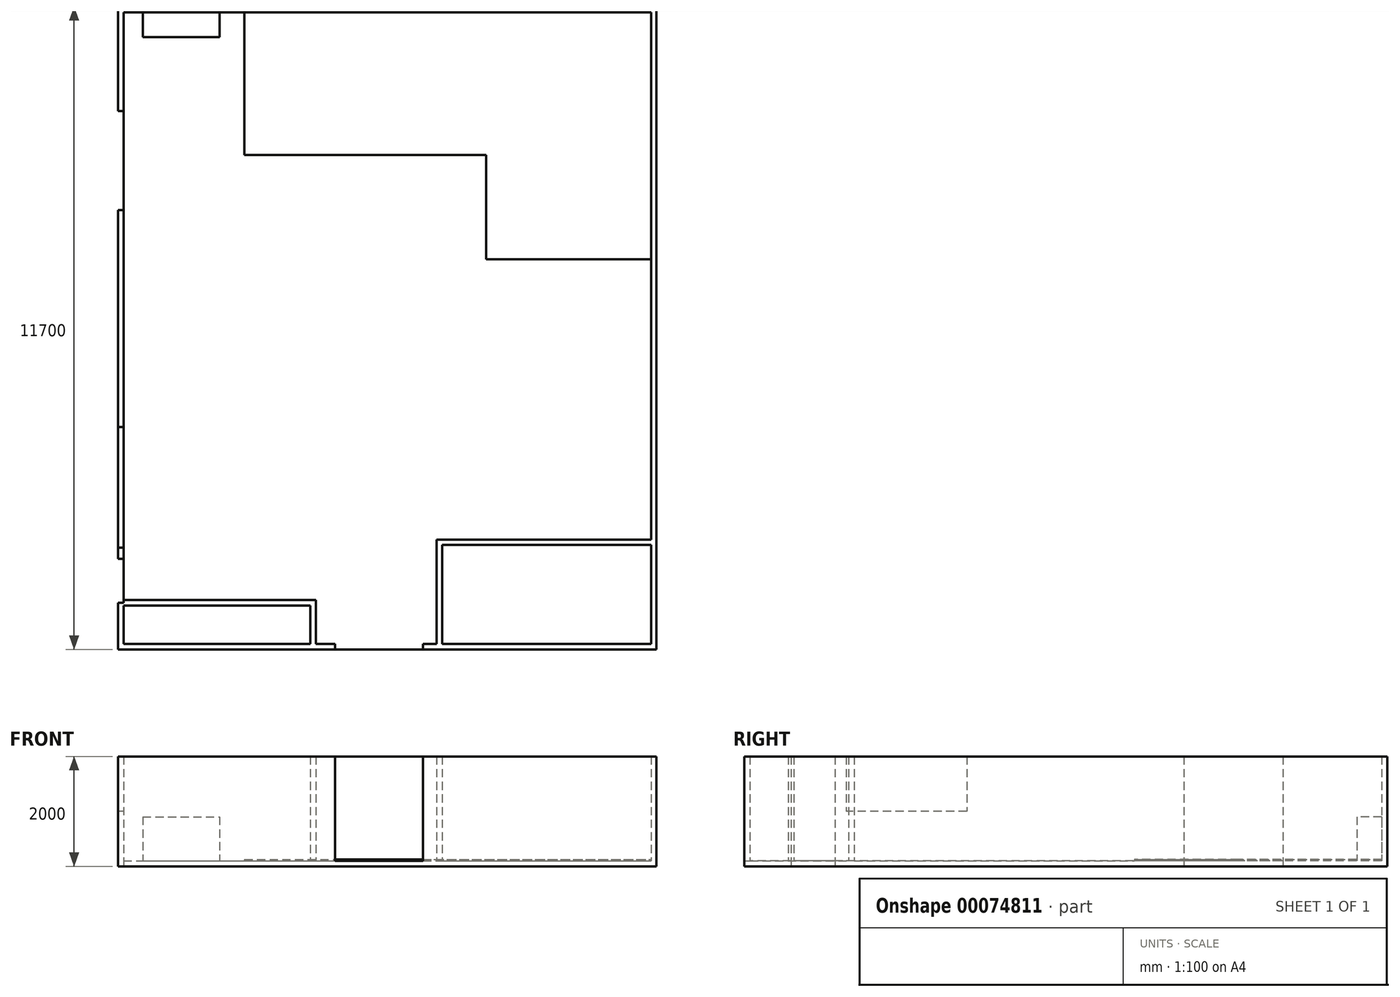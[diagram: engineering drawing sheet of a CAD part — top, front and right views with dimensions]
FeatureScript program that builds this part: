
annotation { "Feature Type Name" : "Feature", "Feature Type Description" : "" }
export const myFeature = defineFeature(function(context is Context, id is Id, definition is map)
    precondition{}
    {
        {
            var Q0;
            Q0=qCreatedBy(makeId("Top.planeOp"),FACE);
            var sketch = newSketch(context, id + "F0", { "sketchPlane" : qUnion([Q0])});
            skLineSegment(sketch, "E0.bottom", {"start": v(-14637.26, 1697.17) * mm, "end": v(-4837.26, 1697.17) * mm});
            skLineSegment(sketch, "E0.top", {"start": v(-14637.26, -10002.83) * mm, "end": v(-4837.26, -10002.83) * mm});
            skLineSegment(sketch, "E0.left", {"start": v(-14637.26, 1697.17) * mm, "end": v(-14637.26, -10002.83) * mm});
            skLineSegment(sketch, "E0.right", {"start": v(-4837.26, 1697.17) * mm, "end": v(-4837.26, -10002.83) * mm});
            skLineSegment(sketch, "E1.top", {"start": v(-8937.26, -10002.83) * mm, "end": v(-4837.26, -10002.83) * mm});
            skLineSegment(sketch, "E1.right", {"start": v(-4837.26, -8102.83) * mm, "end": v(-4837.26, -10002.83) * mm});
            skLineSegment(sketch, "E2.top", {"start": v(-11137.26, -10002.83) * mm, "end": v(-14637.26, -10002.83) * mm});
            skLineSegment(sketch, "E2.right", {"start": v(-14637.26, -9202.83) * mm, "end": v(-14637.26, -10002.83) * mm});
            skSolve(sketch);
        }
        {
            var Q0;
            Q0 = qSketchRegion(id + "F0", true);
            extrude(context, id + "F1", {"entities" : qUnion([Q0]), "depth" : 100 * mm});
        }
        {
            var Q0;
            Q0=makeQuery(id+"F1.opExtrude","CAP_FACE",FACE,{"disambiguationData":[OSD([sQuery(id+"F0.wireOp",EDGE,"E0.bottom"),sQuery(id+"F0.wireOp",EDGE,"E0.top"),sQuery(id+"F0.wireOp",EDGE,"E0.left"),sQuery(id+"F0.wireOp",EDGE,"E0.right"),sQuery(id+"F0.wireOp",EDGE,"E1.top"),sQuery(id+"F0.wireOp",EDGE,"E1.right"),sQuery(id+"F0.wireOp",EDGE,"E2.top"),sQuery(id+"F0.wireOp",EDGE,"E2.right")])],"isStart":false});
            var sketch = newSketch(context, id + "F2", { "sketchPlane" : qUnion([Q0])});
            skLineSegment(sketch, "E3.bottom", {"start": v(-14637.26, -10002.83) * mm, "end": v(-10890.72, -10002.83) * mm});
            skLineSegment(sketch, "E3.left", {"start": v(-14637.26, -10002.83) * mm, "end": v(-14637.26, -9155.58) * mm});
            skLineSegment(sketch, "E4.bottom", {"start": v(-4837.26, -10002.83) * mm, "end": v(-8666.1, -10002.83) * mm});
            skLineSegment(sketch, "E4.left", {"start": v(-4837.26, -10002.83) * mm, "end": v(-4837.26, -7690.3) * mm});
            skLineSegment(sketch, "E5.bottom", {"start": v(-14637.26, 1697.17) * mm, "end": v(-4837.26, 1697.17) * mm});
            skLineSegment(sketch, "E5.top", {"start": v(-14637.26, 1597.17) * mm, "end": v(-4837.26, 1597.17) * mm});
            skLineSegment(sketch, "E5.left", {"start": v(-14637.26, 1697.17) * mm, "end": v(-14637.26, 1597.17) * mm});
            skLineSegment(sketch, "E5.right", {"start": v(-4837.26, 1697.17) * mm, "end": v(-4837.26, 1597.17) * mm});
            skLineSegment(sketch, "E6.bottom", {"start": v(-14637.26, 1597.17) * mm, "end": v(-14537.26, 1597.17) * mm});
            skLineSegment(sketch, "E6.left", {"start": v(-14637.26, 1597.17) * mm, "end": v(-14637.26, -8609.96) * mm});
            skLineSegment(sketch, "E7.top", {"start": v(-5037.26, 1597.17) * mm, "end": v(-4837.26, 1597.17) * mm});
            skLineSegment(sketch, "E7.right", {"start": v(-4837.26, -7344.68) * mm, "end": v(-4837.26, 1597.17) * mm});
            skLineSegment(sketch, "E8.bottom", {"start": v(-14637.26, -10002.83) * mm, "end": v(-4837.26, -10002.83) * mm});
            skLineSegment(sketch, "E8.top", {"start": v(-14637.26, -9902.83) * mm, "end": v(-4837.26, -9902.83) * mm});
            skLineSegment(sketch, "E8.left", {"start": v(-14637.26, -10002.83) * mm, "end": v(-14637.26, -9902.83) * mm});
            skLineSegment(sketch, "E8.right", {"start": v(-4837.26, -10002.83) * mm, "end": v(-4837.26, -9902.83) * mm});
            skLineSegment(sketch, "E9.bottom", {"start": v(-4837.26, -10002.83) * mm, "end": v(-4937.26, -10002.83) * mm});
            skLineSegment(sketch, "E9.top", {"start": v(-4837.26, 1597.17) * mm, "end": v(-4937.26, 1597.17) * mm});
            skLineSegment(sketch, "E9.left", {"start": v(-4837.26, -10002.83) * mm, "end": v(-4837.26, 1597.17) * mm});
            skLineSegment(sketch, "E9.right", {"start": v(-4937.26, -10002.83) * mm, "end": v(-4937.26, 1597.17) * mm});
            skLineSegment(sketch, "E10.top", {"start": v(-14637.26, -9902.83) * mm, "end": v(-14537.26, -9902.83) * mm});
            skLineSegment(sketch, "E10.left", {"start": v(-14637.26, 1597.17) * mm, "end": v(-14637.26, -9902.83) * mm});
            skLineSegment(sketch, "E10.right", {"start": v(-14537.26, 1597.17) * mm, "end": v(-14537.26, -9902.83) * mm});
            skLineSegment(sketch, "E11.top", {"start": v(-14537.26, -9902.83) * mm, "end": v(-11037.26, -9902.83) * mm});
            skLineSegment(sketch, "E11.left", {"start": v(-14537.26, -8902.83) * mm, "end": v(-14537.26, -9902.83) * mm});
            skLineSegment(sketch, "E12.bottom", {"start": v(-9037.26, -9902.83) * mm, "end": v(-4937.26, -9902.83) * mm});
            skLineSegment(sketch, "E12.right", {"start": v(-4937.26, -9902.83) * mm, "end": v(-4937.26, -8002.83) * mm});
            skSolve(sketch);
        }
        {
            var Q0;
            Q0 = qSketchRegion(id + "F2", true);
            extrude(context, id + "F3", {"entities" : qUnion([Q0]), "operationType" : NewBodyOperationType.ADD, "depth" : 1900 * mm});
        }
        {
            var Q0;
            Q0=makeQuery(id+"F1.opExtrude","CAP_FACE",FACE,{"disambiguationData":[OSD([sQuery(id+"F0.wireOp",EDGE,"E0.bottom"),sQuery(id+"F0.wireOp",EDGE,"E0.top"),sQuery(id+"F0.wireOp",EDGE,"E0.left"),sQuery(id+"F0.wireOp",EDGE,"E0.right"),sQuery(id+"F0.wireOp",EDGE,"E1.top"),sQuery(id+"F0.wireOp",EDGE,"E1.right"),sQuery(id+"F0.wireOp",EDGE,"E2.top"),sQuery(id+"F0.wireOp",EDGE,"E2.right")])],"isStart":false});
            var sketch = newSketch(context, id + "F4", { "sketchPlane" : qUnion([Q0])});
            skLineSegment(sketch, "E13.bottom", {"start": v(-8837.26, -8002.83) * mm, "end": v(-8737.26, -8002.83) * mm});
            skLineSegment(sketch, "E13.top", {"start": v(-8837.26, -9902.83) * mm, "end": v(-8737.26, -9902.83) * mm});
            skLineSegment(sketch, "E13.left", {"start": v(-8837.26, -8002.83) * mm, "end": v(-8837.26, -9902.83) * mm});
            skLineSegment(sketch, "E13.right", {"start": v(-8737.26, -8102.83) * mm, "end": v(-8737.26, -9902.83) * mm});
            skLineSegment(sketch, "E14.bottom", {"start": v(-8837.26, -8002.83) * mm, "end": v(-4937.26, -8002.83) * mm});
            skLineSegment(sketch, "E14.top", {"start": v(-8737.26, -8102.83) * mm, "end": v(-4937.26, -8102.83) * mm});
            skLineSegment(sketch, "E14.left", {"start": v(-8837.26, -8102.83) * mm, "end": v(-8837.26, -8002.83) * mm});
            skLineSegment(sketch, "E14.right", {"start": v(-4937.26, -8102.83) * mm, "end": v(-4937.26, -8002.83) * mm});
            skLineSegment(sketch, "E15.bottom", {"start": v(-14537.26, -9102.83) * mm, "end": v(-11137.26, -9102.83) * mm});
            skLineSegment(sketch, "E15.top", {"start": v(-14537.26, -9202.83) * mm, "end": v(-11137.26, -9202.83) * mm});
            skLineSegment(sketch, "E15.left", {"start": v(-14537.26, -9102.83) * mm, "end": v(-14537.26, -9202.83) * mm});
            skLineSegment(sketch, "E16.bottom", {"start": v(-11037.26, -9902.83) * mm, "end": v(-11137.26, -9902.83) * mm});
            skLineSegment(sketch, "E16.top", {"start": v(-11037.26, -9102.83) * mm, "end": v(-11137.26, -9102.83) * mm});
            skLineSegment(sketch, "E16.left", {"start": v(-11037.26, -9902.83) * mm, "end": v(-11037.26, -9102.83) * mm});
            skLineSegment(sketch, "E16.right", {"start": v(-11137.26, -9902.83) * mm, "end": v(-11137.26, -9202.83) * mm});
            skSolve(sketch);
        }
        {
            var Q0;
            Q0=makeQuery(id+"F4.imprint","IMPRINT",FACE,{"disambiguationData":[TD([[makeQuery(id+"F4.imprint","IMPRINT",EDGE,{"derivedFrom":sQuery(id+"F4.wireOp",EDGE,"E15.bottom")}),-1.0]])]});
            var Q1;
            Q1=makeQuery(id+"F4.imprint","IMPRINT",FACE,{"disambiguationData":[TD([[makeQuery(id+"F4.imprint","IMPRINT",EDGE,{"derivedFrom":sQuery(id+"F4.wireOp",EDGE,"E13.top")}),1.0]])]});
            extrude(context, id + "F5", {"entities" : qUnion([Q0, Q1]), "operationType" : NewBodyOperationType.ADD, "depth" : 1900 * mm});
        }
        {
            var Q0;
            Q0=makeQuery(id+"F3.boolean.opBoolean","MERGE",FACE,{"derivedFrom":[makeQuery(id+"F1.opExtrude","SWEPT_FACE",FACE,{"disambiguationData":[OSD([sQuery(id+"F0.wireOp",EDGE,"E0.left"),sQuery(id+"F0.wireOp",EDGE,"E2.right")])]}),makeQuery(id+"F3.opExtrude","SWEPT_FACE",FACE,{"disambiguationData":[OSD([sQuery(id+"F2.wireOp",EDGE,"E5.left"),sQuery(id+"F2.wireOp",EDGE,"E8.left"),sQuery(id+"F2.wireOp",EDGE,"E10.left")])]})]});
            var sketch = newSketch(context, id + "F6", { "sketchPlane" : qUnion([Q0])});
            skLineSegment(sketch, "E17.bottom", {"start": v(202.83, 2000) * mm, "end": v(2002.83, 2000) * mm});
            skLineSegment(sketch, "E17.top", {"start": v(202.83, 0) * mm, "end": v(2002.83, 0) * mm});
            skLineSegment(sketch, "E17.left", {"start": v(202.83, 2000) * mm, "end": v(202.83, 0) * mm});
            skLineSegment(sketch, "E17.right", {"start": v(2002.83, 2000) * mm, "end": v(2002.83, 0) * mm});
            skLineSegment(sketch, "E18.bottom", {"start": v(8352.83, 2000) * mm, "end": v(9152.83, 2000) * mm});
            skLineSegment(sketch, "E18.top", {"start": v(8352.83, 0) * mm, "end": v(9152.83, 0) * mm});
            skLineSegment(sketch, "E18.left", {"start": v(8352.83, 2000) * mm, "end": v(8352.83, 0) * mm});
            skLineSegment(sketch, "E18.right", {"start": v(9152.83, 2000) * mm, "end": v(9152.83, 0) * mm});
            skLineSegment(sketch, "E19.bottom", {"start": v(5952.83, 2000) * mm, "end": v(8152.83, 2000) * mm});
            skLineSegment(sketch, "E19.top", {"start": v(5952.83, 1000) * mm, "end": v(8152.83, 1000) * mm});
            skLineSegment(sketch, "E19.left", {"start": v(5952.83, 2000) * mm, "end": v(5952.83, 1000) * mm});
            skLineSegment(sketch, "E19.right", {"start": v(8152.83, 2000) * mm, "end": v(8152.83, 1000) * mm});
            skSolve(sketch);
        }
        {
            var Q0;
            Q0 = qSketchRegion(id + "F6", true);
            extrude(context, id + "F7", {"entities" : qUnion([Q0]), "operationType" : NewBodyOperationType.REMOVE, "oppositeDirection" : true, "depth" : 100 * mm});
        }
        {
            var Q0;
            {var subQ0=sQuery(id+"F2.wireOp",EDGE,"E12.bottom");var subQ1=sQuery(id+"F2.wireOp",EDGE,"E11.top");var subQ2=sQuery(id+"F2.wireOp",EDGE,"E8.top");var subQ5=sQuery(id+"F4.wireOp",EDGE,"E16.left");Q0=makeQuery(id+"F5.boolean.opBoolean","SPLIT",FACE,{"disambiguationData":[TD([makeQuery(id+"F5.opExtrude","SWEPT_FACE",FACE,{"disambiguationData":[OSD([subQ5])]})])],"derivedFrom":makeQuery(id+"F3.opExtrude","SWEPT_FACE",FACE,{"disambiguationData":[OSD([subQ2,subQ1,subQ0])]})});}
            var sketch = newSketch(context, id + "F8", { "sketchPlane" : qUnion([Q0])});
            skLineSegment(sketch, "E20.bottom", {"start": v(9087.26, 2100) * mm, "end": v(10687.26, 2100) * mm});
            skLineSegment(sketch, "E20.top", {"start": v(9087.26, 100) * mm, "end": v(10687.26, 100) * mm});
            skLineSegment(sketch, "E20.left", {"start": v(9087.26, 2100) * mm, "end": v(9087.26, 100) * mm});
            skLineSegment(sketch, "E20.right", {"start": v(10687.26, 2100) * mm, "end": v(10687.26, 100) * mm});
            skSolve(sketch);
        }
        {
            var Q0;
            Q0 = qSketchRegion(id + "F8", true);
            extrude(context, id + "F9", {"entities" : qUnion([Q0]), "operationType" : NewBodyOperationType.REMOVE, "oppositeDirection" : true, "depth" : 100 * mm});
        }
        {
            var Q0;
            Q0=makeQuery(id+"F9.boolean.opBoolean","MERGE",FACE,{"derivedFrom":[makeQuery(id+"F5.boolean.opBoolean","SPLIT",FACE,{"disambiguationData":[TD([makeQuery(id+"F5.opExtrude","SWEPT_FACE",FACE,{"disambiguationData":[OSD([sQuery(id+"F4.wireOp",EDGE,"E14.bottom")])]})])],"derivedFrom":makeQuery(id+"F1.opExtrude","CAP_FACE",FACE,{"disambiguationData":[OSD([sQuery(id+"F0.wireOp",EDGE,"E0.bottom"),sQuery(id+"F0.wireOp",EDGE,"E0.top"),sQuery(id+"F0.wireOp",EDGE,"E0.left"),sQuery(id+"F0.wireOp",EDGE,"E0.right"),sQuery(id+"F0.wireOp",EDGE,"E1.top"),sQuery(id+"F0.wireOp",EDGE,"E1.right"),sQuery(id+"F0.wireOp",EDGE,"E2.top"),sQuery(id+"F0.wireOp",EDGE,"E2.right")])],"isStart":false})}),makeQuery(id+"F9.opExtrude","SWEPT_FACE",FACE,{"disambiguationData":[OSD([sQuery(id+"F8.wireOp",EDGE,"E20.top")])]})]});
            var sketch = newSketch(context, id + "F10", { "sketchPlane" : qUnion([Q0])});
            skLineSegment(sketch, "E21.bottom", {"start": v(-7937.26, 1597.17) * mm, "end": v(-4937.26, 1597.17) * mm});
            skLineSegment(sketch, "E21.top", {"start": v(-7937.26, -2902.83) * mm, "end": v(-4937.26, -2902.83) * mm});
            skLineSegment(sketch, "E21.left", {"start": v(-7937.26, 1597.17) * mm, "end": v(-7937.26, -2902.83) * mm});
            skLineSegment(sketch, "E21.right", {"start": v(-4937.26, 1597.17) * mm, "end": v(-4937.26, -2902.83) * mm});
            skLineSegment(sketch, "E22.bottom", {"start": v(-12337.26, 1597.17) * mm, "end": v(-7937.26, 1597.17) * mm});
            skLineSegment(sketch, "E22.top", {"start": v(-12337.26, -1002.83) * mm, "end": v(-7937.26, -1002.83) * mm});
            skLineSegment(sketch, "E22.left", {"start": v(-12337.26, 1597.17) * mm, "end": v(-12337.26, -1002.83) * mm});
            skLineSegment(sketch, "E22.right", {"start": v(-7937.26, 1597.17) * mm, "end": v(-7937.26, -1002.83) * mm});
            skSolve(sketch);
        }
        {
            var Q0;
            Q0=makeQuery(id+"F10.imprint","IMPRINT",FACE,{"disambiguationData":[TD([[makeQuery(id+"F10.imprint","IMPRINT",EDGE,{"derivedFrom":sQuery(id+"F10.wireOp",EDGE,"E22.bottom")}),-1.0]])]});
            var Q1;
            Q1=makeQuery(id+"F10.imprint","IMPRINT",FACE,{"disambiguationData":[TD([[makeQuery(id+"F10.imprint","IMPRINT",EDGE,{"derivedFrom":sQuery(id+"F10.wireOp",EDGE,"E21.bottom")}),-1.0]])]});
            extrude(context, id + "F11", {"entities" : qUnion([Q0, Q1]), "operationType" : NewBodyOperationType.ADD, "depth" : 25 * mm});
        }
        {
            var Q0;
            Q0=makeQuery(id+"F9.boolean.opBoolean","MERGE",FACE,{"derivedFrom":[makeQuery(id+"F5.boolean.opBoolean","SPLIT",FACE,{"disambiguationData":[TD([makeQuery(id+"F5.opExtrude","SWEPT_FACE",FACE,{"disambiguationData":[OSD([sQuery(id+"F4.wireOp",EDGE,"E14.bottom")])]})])],"derivedFrom":makeQuery(id+"F1.opExtrude","CAP_FACE",FACE,{"disambiguationData":[OSD([sQuery(id+"F0.wireOp",EDGE,"E0.bottom"),sQuery(id+"F0.wireOp",EDGE,"E0.top"),sQuery(id+"F0.wireOp",EDGE,"E0.left"),sQuery(id+"F0.wireOp",EDGE,"E0.right"),sQuery(id+"F0.wireOp",EDGE,"E1.top"),sQuery(id+"F0.wireOp",EDGE,"E1.right"),sQuery(id+"F0.wireOp",EDGE,"E2.top"),sQuery(id+"F0.wireOp",EDGE,"E2.right")])],"isStart":false})}),makeQuery(id+"F9.opExtrude","SWEPT_FACE",FACE,{"disambiguationData":[OSD([sQuery(id+"F8.wireOp",EDGE,"E20.top")])]})]});
            var sketch = newSketch(context, id + "F12", { "sketchPlane" : qUnion([Q0])});
            skLineSegment(sketch, "E23.bottom", {"start": v(-14188.25, 1597.17) * mm, "end": v(-12788.25, 1597.17) * mm});
            skLineSegment(sketch, "E23.top", {"start": v(-14188.25, 1147.17) * mm, "end": v(-12788.25, 1147.17) * mm});
            skLineSegment(sketch, "E23.left", {"start": v(-14188.25, 1597.17) * mm, "end": v(-14188.25, 1147.17) * mm});
            skLineSegment(sketch, "E23.right", {"start": v(-12788.25, 1597.17) * mm, "end": v(-12788.25, 1147.17) * mm});
            skSolve(sketch);
        }
        {
            var Q0;
            Q0 = qSketchRegion(id + "F12", true);
            extrude(context, id + "F13", {"entities" : qUnion([Q0]), "operationType" : NewBodyOperationType.ADD, "depth" : 800 * mm});
        }
    });
